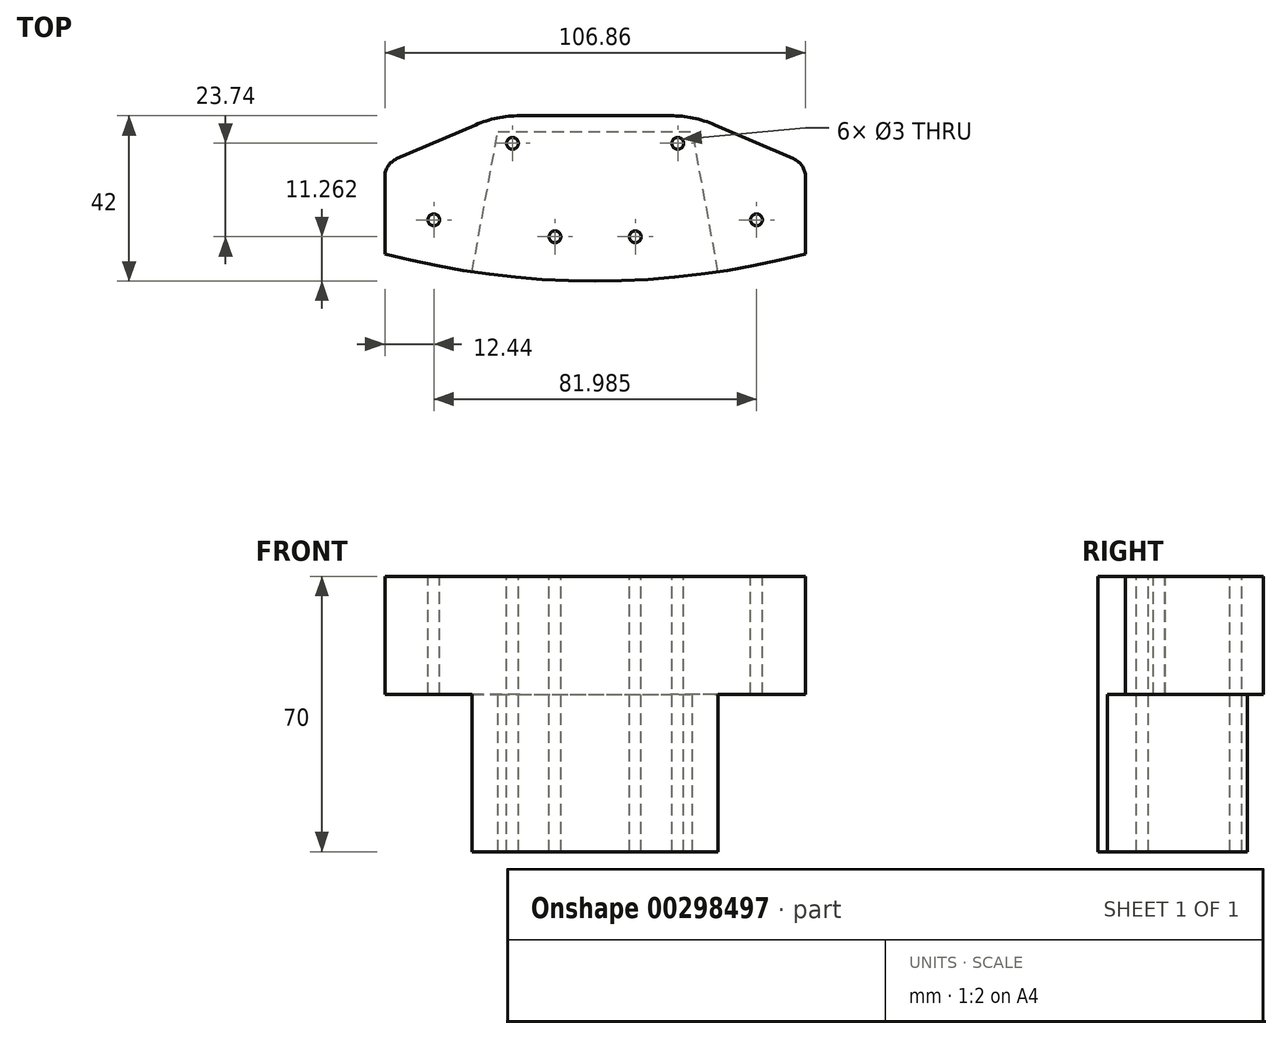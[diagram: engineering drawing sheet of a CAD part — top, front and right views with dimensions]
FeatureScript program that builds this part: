
annotation { "Feature Type Name" : "Feature", "Feature Type Description" : "" }
export const myFeature = defineFeature(function(context is Context, id is Id, definition is map)
    precondition{}
    {
        {
            var Q0;
            Q0=qCreatedBy(makeId("Top.planeOp"),FACE);
            var sketch = newSketch(context, id + "F0", { "sketchPlane" : qUnion([Q0])});
            skArc(sketch, "E0", {"start": v(-53.43, -203.09) * mm, "mid": v(0, -210) * mm, "end": v(53.43, -203.09) * mm});
            skLineSegment(sketch, "E1", {"start": v(0, 0) * mm, "end": v(-114.72, 0) * mm, "construction": true});
            skLineSegment(sketch, "E2", {"start": v(0, 0) * mm, "end": v(0, 25) * mm, "construction": true});
            skLineSegment(sketch, "E3", {"start": v(0, -188) * mm, "end": v(0, -168) * mm, "construction": true});
            skLineSegment(sketch, "E4", {"start": v(0, -168) * mm, "end": v(25, -168) * mm});
            skLineSegment(sketch, "E5", {"start": v(25, -168) * mm, "end": v(53.43, -180.25) * mm});
            skLineSegment(sketch, "E6.MirrorCS", {"start": v(0, -168) * mm, "end": v(-25, -168) * mm});
            skLineSegment(sketch, "E7.MirrorCS", {"start": v(-25, -168) * mm, "end": v(-53.43, -180.25) * mm});
            skPoint(sketch, "E8.orphan", {"position": v(0, 25) * mm});
            skLineSegment(sketch, "E9", {"start": v(-53.43, -180.25) * mm, "end": v(-53.43, -203.09) * mm});
            skLineSegment(sketch, "E10", {"start": v(53.43, -180.25) * mm, "end": v(53.43, -203.09) * mm});
            skSolve(sketch);
        }
        {
            var Q0;
            Q0=qSketchRegion(id+"F0",true);
            extrude(context, id + "F1", {"entities" : qUnion([Q0]), "depth" : 30 * mm});
        }
        {
            var Q0;
            Q0=makeQuery(id+"F1.opExtrude","CAP_FACE",FACE,{"disambiguationData":[OSD([sQuery(id+"F0.wireOp",EDGE,"zaacHSxv-Ykmp-iado-Lf9L-hkywlrfjUfpX"),sQuery(id+"F0.wireOp",EDGE,"E0"),sQuery(id+"F0.wireOp",EDGE,"l4xIi2As-Ueo2-zj1L-4dbT-WmD2rElXbqZN"),sQuery(id+"F0.wireOp",EDGE,"cd5aeadf-9b7c-4279-ad70-133639c7d9530.MirrorCS"),sQuery(id+"F0.wireOp",EDGE,"E4"),sQuery(id+"F0.wireOp",EDGE,"E5"),sQuery(id+"F0.wireOp",EDGE,"E6.MirrorCS"),sQuery(id+"F0.wireOp",EDGE,"E7.MirrorCS"),sQuery(id+"F0.wireOp",EDGE,"d7c433af-e9a5-42f2-8bff-84c690de4411.trimOffspring")])],"isStart":false});
            var sketch = newSketch(context, id + "F2", { "sketchPlane" : qUnion([Q0])});
            skArc(sketch, "E11.0", {"start": v(-198.1, 18.95) * mm, "mid": v(0, -199) * mm, "end": v(198.1, 18.95) * mm, "construction": true});
            skCircle(sketch, "E12.1.0", {"center": v(-61.5, -189.11) * mm, "radius": 1.5 * mm});
            skCircle(sketch, "E12.2.0", {"center": v(-116.97, -160.85) * mm, "radius": 1.5 * mm});
            skCircle(sketch, "E12.3.0", {"center": v(-161, -116.83) * mm, "radius": 1.5 * mm});
            skCircle(sketch, "E12.4.0", {"center": v(-189.27, -61.36) * mm, "radius": 1.5 * mm});
            skCircle(sketch, "E12.5.0", {"center": v(-199.02, 0.13) * mm, "radius": 1.5 * mm});
            skPoint(sketch, "E12.center", {"position": v(-0.02, 0.15) * mm});
            skLineSegment(sketch, "E12.anchor1", {"start": v(-0.02, 0.15) * mm, "end": v(0, -199) * mm, "construction": true});
            skLineSegment(sketch, "E12.anchor2", {"start": v(-0.02, 0.15) * mm, "end": v(-199.02, 0.13) * mm, "construction": true});
            skCircle(sketch, "E13.MirrorC", {"center": v(61.5, -189.1) * mm, "radius": 1.5 * mm});
            skCircle(sketch, "E14.MirrorC", {"center": v(116.97, -160.83) * mm, "radius": 1.5 * mm});
            skCircle(sketch, "E15.MirrorC", {"center": v(160.99, -116.8) * mm, "radius": 1.5 * mm});
            skCircle(sketch, "E16.MirrorC", {"center": v(189.25, -61.32) * mm, "radius": 1.5 * mm});
            skCircle(sketch, "E17.MirrorC", {"center": v(198.98, 0.18) * mm, "radius": 1.5 * mm});
            skLineSegment(sketch, "E18", {"start": v(0, -175) * mm, "end": v(-21, -175) * mm, "construction": true});
            skCircle(sketch, "E19", {"center": v(-21, -175) * mm, "radius": 1.5 * mm});
            skLineSegment(sketch, "E20", {"start": v(-21, -175) * mm, "end": v(-21, -195) * mm, "construction": true});
            skLineSegment(sketch, "E21", {"start": v(-21, -195) * mm, "end": v(-41, -194.45) * mm, "construction": true});
            skCircle(sketch, "E22", {"center": v(-41, -194.45) * mm, "radius": 1.5 * mm});
            skCircle(sketch, "E23", {"center": v(-10.2, -198.74) * mm, "radius": 1.5 * mm});
            skCircle(sketch, "E24.MirrorC", {"center": v(21, -175) * mm, "radius": 1.5 * mm});
            skCircle(sketch, "E25.MirrorC", {"center": v(10.2, -198.74) * mm, "radius": 1.5 * mm});
            skCircle(sketch, "E26.MirrorC", {"center": v(41, -194.44) * mm, "radius": 1.5 * mm});
            skSolve(sketch);
        }
        {
            var Q0;
            Q0=qSketchRegion(id+"F2",true);
            extrude(context, id + "F3", {"entities" : qUnion([Q0]), "operationType" : NewBodyOperationType.REMOVE, "endBound" : BoundingType.THROUGH_ALL, "oppositeDirection" : true, "depth" : 25 * mm});
        }
        {
            var Q0;
            Q0=makeQuery(id+"F1.opExtrude","SWEPT_EDGE",EDGE,{"disambiguationData":[OSD([sQuery(id+"F0.wireOp",EDGE,"E4"),sQuery(id+"F0.wireOp",EDGE,"E5")])]});
            var Q1;
            Q1=makeQuery(id+"F1.opExtrude","SWEPT_EDGE",EDGE,{"disambiguationData":[OSD([sQuery(id+"F0.wireOp",EDGE,"E6.MirrorCS"),sQuery(id+"F0.wireOp",EDGE,"E7.MirrorCS")])]});
            fillet(context, id + "F4", {"entities" : qUnion([Q0, Q1]), "radius" : 28.52 * mm, "tangentPropagation" : true, "allowEdgeOverflow" : false});
        }
        {
            var Q0;
            Q0=makeQuery(id+"F1.opExtrude","SWEPT_EDGE",EDGE,{"disambiguationData":[OSD([sQuery(id+"F0.wireOp",EDGE,"E5"),sQuery(id+"F0.wireOp",EDGE,"d7c433af-e9a5-42f2-8bff-84c690de4411.trimOffspring")])]});
            var Q1;
            Q1=makeQuery(id+"F1.opExtrude","SWEPT_EDGE",EDGE,{"disambiguationData":[OSD([sQuery(id+"F0.wireOp",EDGE,"zaacHSxv-Ykmp-iado-Lf9L-hkywlrfjUfpX"),sQuery(id+"F0.wireOp",EDGE,"E7.MirrorCS")])]});
            fillet(context, id + "F5", {"entities" : qUnion([Q0, Q1]), "radius" : 5 * mm, "tangentPropagation" : true, "allowEdgeOverflow" : false});
        }
        {
            var Q0;
            Q0=qCreatedBy(makeId("Top.planeOp"),FACE);
            var sketch = newSketch(context, id + "F6", { "sketchPlane" : qUnion([Q0])});
            skLineSegment(sketch, "E27", {"start": v(0, 0) * mm, "end": v(174.2, -171.38) * mm, "construction": true});
            skLineSegment(sketch, "E28", {"start": v(0, 0) * mm, "end": v(0, 36.6) * mm, "construction": true});
            skLineSegment(sketch, "E29.MirrorCS", {"start": v(0, 0) * mm, "end": v(-174.2, -171.38) * mm, "construction": true});
            skSolve(sketch);
        }
        {
            var Q0;
            Q0=makeQuery(id+"F1.opExtrude","CAP_FACE",FACE,{"disambiguationData":[OSD([sQuery(id+"F0.wireOp",EDGE,"E0"),sQuery(id+"F0.wireOp",EDGE,"E4"),sQuery(id+"F0.wireOp",EDGE,"E5"),sQuery(id+"F0.wireOp",EDGE,"E6.MirrorCS"),sQuery(id+"F0.wireOp",EDGE,"E7.MirrorCS"),sQuery(id+"F0.wireOp",EDGE,"E9"),sQuery(id+"F0.wireOp",EDGE,"E10")])],"isStart":true});
            var sketch = newSketch(context, id + "F7", { "sketchPlane" : qUnion([Q0])});
            skArc(sketch, "E30.0", {"start": v(-31.26, 207.66) * mm, "mid": v(0, 210) * mm, "end": v(31.26, 207.66) * mm});
            skLineSegment(sketch, "E31", {"start": v(31.26, 207.66) * mm, "end": v(24.72, 172.06) * mm});
            skLineSegment(sketch, "E32", {"start": v(24.72, 172.06) * mm, "end": v(0, 172.06) * mm});
            skLineSegment(sketch, "E33.MirrorCS", {"start": v(-24.72, 172.06) * mm, "end": v(0, 172.06) * mm});
            skLineSegment(sketch, "E34.MirrorCS", {"start": v(-31.26, 207.66) * mm, "end": v(-24.72, 172.06) * mm});
            skSolve(sketch);
        }
        {
            var Q0;
            Q0=makeQuery(id+"F7.imprint","IMPRINT",FACE,{"disambiguationData":[TD([[makeQuery(id+"F7.imprint","IMPRINT",EDGE,{"derivedFrom":sQuery(id+"F7.wireOp",EDGE,"E30.0")}),-1.0]])]});
            extrude(context, id + "F8", {"entities" : qUnion([Q0]), "operationType" : NewBodyOperationType.ADD, "depth" : 40 * mm});
        }
    });
